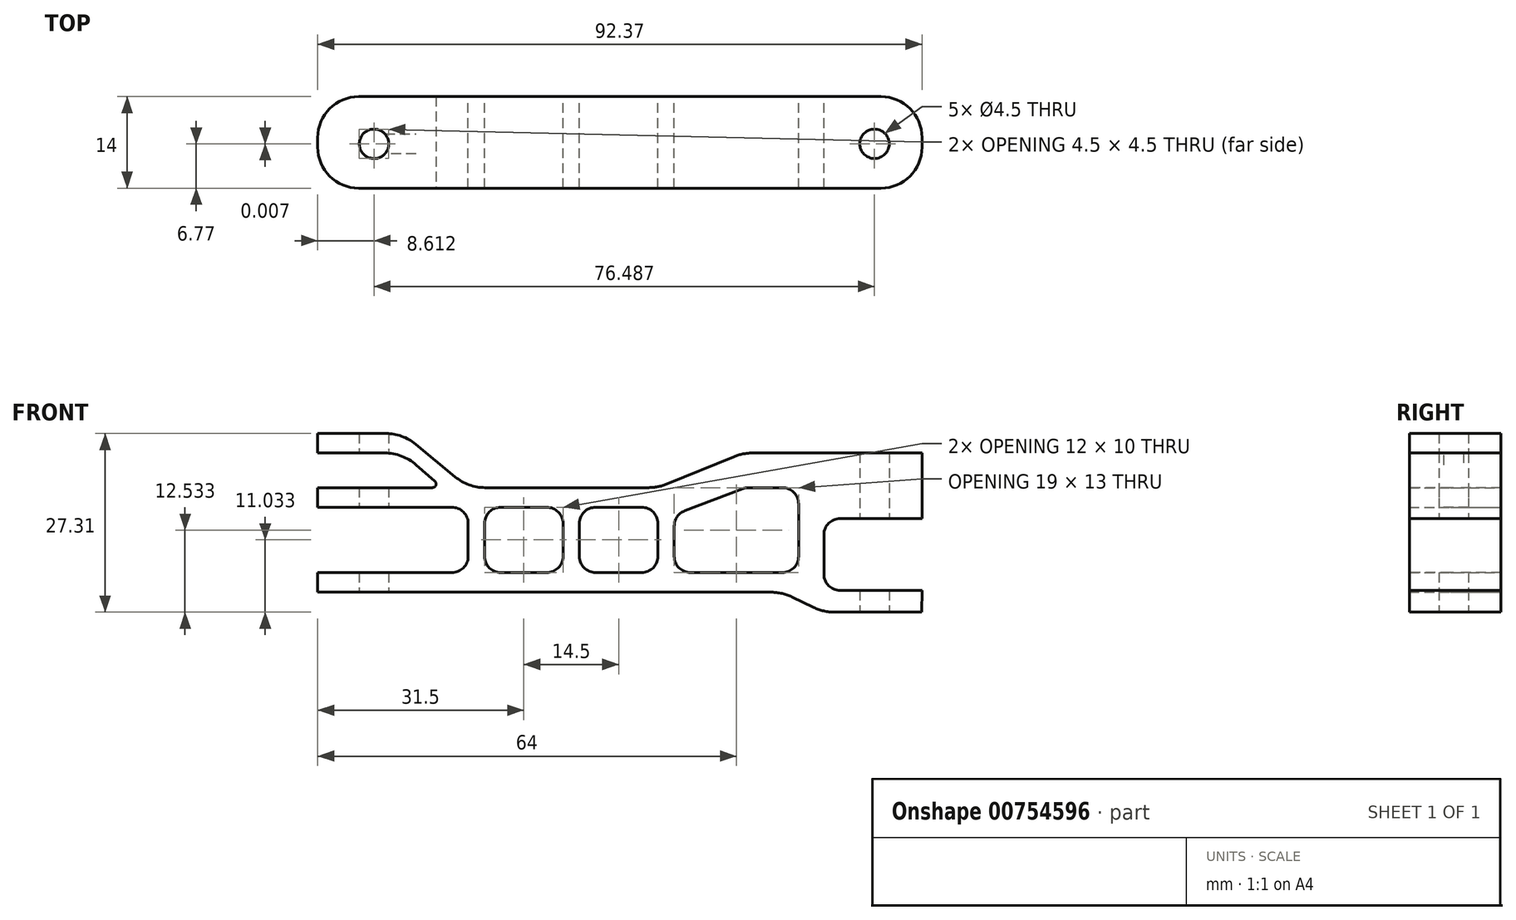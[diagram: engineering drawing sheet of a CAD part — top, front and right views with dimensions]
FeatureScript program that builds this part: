
annotation { "Feature Type Name" : "Feature", "Feature Type Description" : "" }
export const myFeature = defineFeature(function(context is Context, id is Id, definition is map)
    precondition{}
    {
        {
            var Q0;
            Q0=qCreatedBy(makeId("Front.planeOp"),FACE);
            var sketch = newSketch(context, id + "F0", { "sketchPlane" : qUnion([Q0])});
            skLineSegment(sketch, "E0", {"start": v(74.63, 0) * mm, "end": v(59.63, 0) * mm});
            skLineSegment(sketch, "E1", {"start": v(59.63, 0) * mm, "end": v(53.32, 3.03) * mm});
            skLineSegment(sketch, "E2", {"start": v(53.32, 3.03) * mm, "end": v(-17.68, 3.03) * mm});
            skLineSegment(sketch, "E3", {"start": v(-17.68, 3.03) * mm, "end": v(-17.68, 6.03) * mm});
            skLineSegment(sketch, "E4", {"start": v(-17.68, 6.03) * mm, "end": v(5.32, 6.03) * mm});
            skLineSegment(sketch, "E5", {"start": v(5.32, 6.03) * mm, "end": v(5.32, 16.03) * mm});
            skLineSegment(sketch, "E6", {"start": v(5.32, 16.03) * mm, "end": v(-17.68, 16.03) * mm});
            skLineSegment(sketch, "E7", {"start": v(-17.68, 16.03) * mm, "end": v(-17.68, 19.03) * mm});
            skLineSegment(sketch, "E8", {"start": v(-17.68, 19.03) * mm, "end": v(1.32, 19.03) * mm});
            skLineSegment(sketch, "E9", {"start": v(1.32, 19.03) * mm, "end": v(-4.7, 24.31) * mm});
            skLineSegment(sketch, "E10", {"start": v(-4.7, 24.31) * mm, "end": v(-17.68, 24.31) * mm});
            skLineSegment(sketch, "E11", {"start": v(-17.68, 24.31) * mm, "end": v(-17.68, 27.31) * mm});
            skLineSegment(sketch, "E12", {"start": v(-17.68, 27.31) * mm, "end": v(-4.7, 27.31) * mm});
            skLineSegment(sketch, "E13", {"start": v(-4.7, 27.31) * mm, "end": v(5.32, 19.03) * mm});
            skLineSegment(sketch, "E14", {"start": v(5.32, 19.03) * mm, "end": v(34.32, 19.03) * mm});
            skLineSegment(sketch, "E15", {"start": v(34.32, 19.03) * mm, "end": v(47.29, 24.31) * mm});
            skLineSegment(sketch, "E16", {"start": v(47.29, 24.31) * mm, "end": v(74.69, 24.31) * mm});
            skLineSegment(sketch, "E17", {"start": v(74.69, 24.31) * mm, "end": v(74.69, 14.31) * mm});
            skLineSegment(sketch, "E18", {"start": v(74.69, 3.31) * mm, "end": v(74.63, 0) * mm});
            skLineSegment(sketch, "E19", {"start": v(7.82, 16.03) * mm, "end": v(7.82, 6.03) * mm});
            skLineSegment(sketch, "E20", {"start": v(7.82, 6.03) * mm, "end": v(19.82, 6.03) * mm});
            skLineSegment(sketch, "E21", {"start": v(19.82, 6.03) * mm, "end": v(19.82, 16.03) * mm});
            skLineSegment(sketch, "E22", {"start": v(19.82, 16.03) * mm, "end": v(7.82, 16.03) * mm});
            skLineSegment(sketch, "E23", {"start": v(22.32, 16.03) * mm, "end": v(22.32, 6.03) * mm});
            skLineSegment(sketch, "E24", {"start": v(22.32, 6.03) * mm, "end": v(34.32, 6.03) * mm});
            skLineSegment(sketch, "E25", {"start": v(34.32, 6.03) * mm, "end": v(34.32, 16.03) * mm});
            skLineSegment(sketch, "E26", {"start": v(34.32, 16.03) * mm, "end": v(22.32, 16.03) * mm});
            skLineSegment(sketch, "E27", {"start": v(36.82, 6.03) * mm, "end": v(55.82, 6.03) * mm});
            skLineSegment(sketch, "E28", {"start": v(55.82, 6.03) * mm, "end": v(55.82, 19.03) * mm});
            skLineSegment(sketch, "E29", {"start": v(55.82, 19.03) * mm, "end": v(47.74, 19.03) * mm});
            skLineSegment(sketch, "E30", {"start": v(47.74, 19.03) * mm, "end": v(36.82, 14.87) * mm});
            skLineSegment(sketch, "E31", {"start": v(36.82, 14.87) * mm, "end": v(36.82, 6.03) * mm});
            skLineSegment(sketch, "E32", {"start": v(74.69, 14.31) * mm, "end": v(59.69, 14.31) * mm});
            skLineSegment(sketch, "E33", {"start": v(74.69, 3.31) * mm, "end": v(59.69, 3.31) * mm});
            skLineSegment(sketch, "E34", {"start": v(59.69, 3.31) * mm, "end": v(59.69, 14.31) * mm});
            skSolve(sketch);
        }
        {
            var Q0;
            Q0=makeQuery(id+"F0.imprint","IMPRINT",FACE,{"disambiguationData":[TD([[makeQuery(id+"F0.imprint","IMPRINT",EDGE,{"derivedFrom":sQuery(id+"F0.wireOp",EDGE,"E0")}),-1.0]])]});
            extrude(context, id + "F1", {"entities" : qUnion([Q0]), "depth" : 14 * mm, "offsetDistance" : 25 * mm});
        }
        {
            var Q0;
            Q0=qCreatedBy(makeId("Top.planeOp"),FACE);
            var sketch = newSketch(context, id + "F2", { "sketchPlane" : qUnion([Q0])});
            skCircle(sketch, "E35", {"center": v(-9.07, -7.23) * mm, "radius": 2.25 * mm});
            skCircle(sketch, "E36", {"center": v(67.42, -7.22) * mm, "radius": 2.25 * mm});
            skSolve(sketch);
        }
        {
            var Q0;
            Q0 = qSketchRegion(id + "F2", true);
            extrude(context, id + "F3", {"entities" : qUnion([Q0]), "operationType" : NewBodyOperationType.REMOVE, "depth" : 99.1 * mm, "offsetDistance" : 25 * mm});
        }
        {
            var Q0;
            Q0 = qSketchRegion(id + "F2", true);
            extrude(context, id + "F4", {"entities" : qUnion([Q0]), "operationType" : NewBodyOperationType.REMOVE, "oppositeDirection" : true, "depth" : 25 * mm, "offsetDistance" : 25 * mm});
        }
        {
            var Q0;
            Q0=makeQuery(id+"F1.opExtrude","CAP_EDGE",EDGE,{"disambiguationData":[OSD([sQuery(id+"F0.wireOp",EDGE,"E11")])],"isStart":false});
            var Q1;
            Q1=makeQuery(id+"F1.opExtrude","CAP_EDGE",EDGE,{"disambiguationData":[OSD([sQuery(id+"F0.wireOp",EDGE,"E11")])],"isStart":true});
            var Q2;
            Q2=makeQuery(id+"F1.opExtrude","CAP_EDGE",EDGE,{"disambiguationData":[OSD([sQuery(id+"F0.wireOp",EDGE,"E7")])],"isStart":false});
            var Q3;
            Q3=makeQuery(id+"F1.opExtrude","CAP_EDGE",EDGE,{"disambiguationData":[OSD([sQuery(id+"F0.wireOp",EDGE,"E7")])],"isStart":true});
            var Q4;
            Q4=makeQuery(id+"F1.opExtrude","CAP_EDGE",EDGE,{"disambiguationData":[OSD([sQuery(id+"F0.wireOp",EDGE,"E3")])],"isStart":true});
            var Q5;
            Q5=makeQuery(id+"F1.opExtrude","CAP_EDGE",EDGE,{"disambiguationData":[OSD([sQuery(id+"F0.wireOp",EDGE,"E3")])],"isStart":false});
            fillet(context, id + "F5", {"entities" : qUnion([Q0, Q1, Q2, Q3, Q4, Q5]), "radius" : 6.28 * mm, "tangentPropagation" : true, "allowEdgeOverflow" : false});
        }
        {
            var Q0;
            Q0=makeQuery(id+"F1.opExtrude","CAP_EDGE",EDGE,{"disambiguationData":[OSD([sQuery(id+"F0.wireOp",EDGE,"E17")])],"isStart":false});
            var Q1;
            Q1=makeQuery(id+"F1.opExtrude","CAP_EDGE",EDGE,{"disambiguationData":[OSD([sQuery(id+"F0.wireOp",EDGE,"E17")])],"isStart":true});
            var Q2;
            Q2=makeQuery(id+"F1.opExtrude","CAP_EDGE",EDGE,{"disambiguationData":[OSD([sQuery(id+"F0.wireOp",EDGE,"E18")])],"isStart":false});
            var Q3;
            Q3=makeQuery(id+"F1.opExtrude","CAP_EDGE",EDGE,{"disambiguationData":[OSD([sQuery(id+"F0.wireOp",EDGE,"E18")])],"isStart":true});
            fillet(context, id + "F6", {"entities" : qUnion([Q0, Q1, Q2, Q3]), "radius" : 6.28 * mm, "tangentPropagation" : true, "allowEdgeOverflow" : false});
        }
        {
            var Q0;
            Q0=makeQuery(id+"F1.opExtrude","SWEPT_EDGE",EDGE,{"disambiguationData":[OSD([sQuery(id+"F0.wireOp",EDGE,"E27"),sQuery(id+"F0.wireOp",EDGE,"E31")])]});
            var Q1;
            Q1=makeQuery(id+"F1.opExtrude","SWEPT_EDGE",EDGE,{"disambiguationData":[OSD([sQuery(id+"F0.wireOp",EDGE,"E30"),sQuery(id+"F0.wireOp",EDGE,"E31")])]});
            var Q2;
            Q2=makeQuery(id+"F1.opExtrude","SWEPT_EDGE",EDGE,{"disambiguationData":[OSD([sQuery(id+"F0.wireOp",EDGE,"E29"),sQuery(id+"F0.wireOp",EDGE,"E30")])]});
            var Q3;
            Q3=makeQuery(id+"F1.opExtrude","SWEPT_EDGE",EDGE,{"disambiguationData":[OSD([sQuery(id+"F0.wireOp",EDGE,"E28"),sQuery(id+"F0.wireOp",EDGE,"E29")])]});
            var Q4;
            Q4=makeQuery(id+"F1.opExtrude","SWEPT_EDGE",EDGE,{"disambiguationData":[OSD([sQuery(id+"F0.wireOp",EDGE,"E27"),sQuery(id+"F0.wireOp",EDGE,"E28")])]});
            fillet(context, id + "F7", {"entities" : qUnion([Q0, Q1, Q2, Q3, Q4]), "radius" : 2.5 * mm, "tangentPropagation" : true, "allowEdgeOverflow" : false});
        }
        {
            var Q0;
            Q0=makeQuery(id+"F1.opExtrude","SWEPT_EDGE",EDGE,{"disambiguationData":[OSD([sQuery(id+"F0.wireOp",EDGE,"E25"),sQuery(id+"F0.wireOp",EDGE,"E26")])]});
            var Q1;
            Q1=makeQuery(id+"F1.opExtrude","SWEPT_EDGE",EDGE,{"disambiguationData":[OSD([sQuery(id+"F0.wireOp",EDGE,"E23"),sQuery(id+"F0.wireOp",EDGE,"E26")])]});
            var Q2;
            Q2=makeQuery(id+"F1.opExtrude","SWEPT_EDGE",EDGE,{"disambiguationData":[OSD([sQuery(id+"F0.wireOp",EDGE,"E23"),sQuery(id+"F0.wireOp",EDGE,"E24")])]});
            var Q3;
            Q3=makeQuery(id+"F1.opExtrude","SWEPT_EDGE",EDGE,{"disambiguationData":[OSD([sQuery(id+"F0.wireOp",EDGE,"E24"),sQuery(id+"F0.wireOp",EDGE,"E25")])]});
            fillet(context, id + "F8", {"entities" : qUnion([Q0, Q1, Q2, Q3]), "radius" : 2.5 * mm, "tangentPropagation" : true, "allowEdgeOverflow" : false});
        }
        {
            var Q0;
            Q0=makeQuery(id+"F1.opExtrude","SWEPT_EDGE",EDGE,{"disambiguationData":[OSD([sQuery(id+"F0.wireOp",EDGE,"E21"),sQuery(id+"F0.wireOp",EDGE,"E22")])]});
            var Q1;
            Q1=makeQuery(id+"F1.opExtrude","SWEPT_EDGE",EDGE,{"disambiguationData":[OSD([sQuery(id+"F0.wireOp",EDGE,"E19"),sQuery(id+"F0.wireOp",EDGE,"E22")])]});
            var Q2;
            Q2=makeQuery(id+"F1.opExtrude","SWEPT_EDGE",EDGE,{"disambiguationData":[OSD([sQuery(id+"F0.wireOp",EDGE,"E19"),sQuery(id+"F0.wireOp",EDGE,"E20")])]});
            var Q3;
            Q3=makeQuery(id+"F1.opExtrude","SWEPT_EDGE",EDGE,{"disambiguationData":[OSD([sQuery(id+"F0.wireOp",EDGE,"E20"),sQuery(id+"F0.wireOp",EDGE,"E21")])]});
            fillet(context, id + "F9", {"entities" : qUnion([Q0, Q1, Q2, Q3]), "radius" : 2.5 * mm, "tangentPropagation" : true, "allowEdgeOverflow" : false});
        }
        {
            var Q0;
            Q0=makeQuery(id+"F1.opExtrude","SWEPT_EDGE",EDGE,{"disambiguationData":[OSD([sQuery(id+"F0.wireOp",EDGE,"E5"),sQuery(id+"F0.wireOp",EDGE,"E6")])]});
            var Q1;
            Q1=makeQuery(id+"F1.opExtrude","SWEPT_EDGE",EDGE,{"disambiguationData":[OSD([sQuery(id+"F0.wireOp",EDGE,"E4"),sQuery(id+"F0.wireOp",EDGE,"E5")])]});
            var Q2;
            Q2=makeQuery(id+"F1.opExtrude","SWEPT_EDGE",EDGE,{"disambiguationData":[OSD([sQuery(id+"F0.wireOp",EDGE,"E32"),sQuery(id+"F0.wireOp",EDGE,"E34")])]});
            var Q3;
            Q3=makeQuery(id+"F1.opExtrude","SWEPT_EDGE",EDGE,{"disambiguationData":[OSD([sQuery(id+"F0.wireOp",EDGE,"E33"),sQuery(id+"F0.wireOp",EDGE,"E34")])]});
            fillet(context, id + "F10", {"entities" : qUnion([Q0, Q1, Q2, Q3]), "radius" : 2.5 * mm, "tangentPropagation" : true, "allowEdgeOverflow" : false});
        }
        {
            var Q0;
            Q0=makeQuery(id+"F1.opExtrude","SWEPT_EDGE",EDGE,{"disambiguationData":[OSD([sQuery(id+"F0.wireOp",EDGE,"E15"),sQuery(id+"F0.wireOp",EDGE,"E16")])]});
            var Q1;
            Q1=makeQuery(id+"F1.opExtrude","SWEPT_EDGE",EDGE,{"disambiguationData":[OSD([sQuery(id+"F0.wireOp",EDGE,"E14"),sQuery(id+"F0.wireOp",EDGE,"E15")])]});
            var Q2;
            Q2=makeQuery(id+"F1.opExtrude","SWEPT_EDGE",EDGE,{"disambiguationData":[OSD([sQuery(id+"F0.wireOp",EDGE,"E13"),sQuery(id+"F0.wireOp",EDGE,"E14")])]});
            var Q3;
            Q3=makeQuery(id+"F1.opExtrude","SWEPT_EDGE",EDGE,{"disambiguationData":[OSD([sQuery(id+"F0.wireOp",EDGE,"E12"),sQuery(id+"F0.wireOp",EDGE,"E13")])]});
            fillet(context, id + "F11", {"entities" : qUnion([Q0, Q1, Q2, Q3]), "radius" : 7.2 * mm, "tangentPropagation" : true, "allowEdgeOverflow" : false});
        }
        {
            var Q0;
            Q0=makeQuery(id+"F1.opExtrude","SWEPT_EDGE",EDGE,{"disambiguationData":[OSD([sQuery(id+"F0.wireOp",EDGE,"E1"),sQuery(id+"F0.wireOp",EDGE,"E2")])]});
            var Q1;
            Q1=makeQuery(id+"F1.opExtrude","SWEPT_EDGE",EDGE,{"disambiguationData":[OSD([sQuery(id+"F0.wireOp",EDGE,"E0"),sQuery(id+"F0.wireOp",EDGE,"E1")])]});
            fillet(context, id + "F12", {"entities" : qUnion([Q0, Q1]), "radius" : 7.2 * mm, "tangentPropagation" : true, "allowEdgeOverflow" : false});
        }
        {
            var Q0;
            Q0=makeQuery(id+"F1.opExtrude","SWEPT_EDGE",EDGE,{"disambiguationData":[OSD([sQuery(id+"F0.wireOp",EDGE,"E9"),sQuery(id+"F0.wireOp",EDGE,"E10")])]});
            fillet(context, id + "F13", {"entities" : qUnion([Q0]), "radius" : 7.2 * mm, "tangentPropagation" : true, "allowEdgeOverflow" : false});
        }
        {
            var Q0;
            Q0=makeQuery(id+"F1.opExtrude","SWEPT_EDGE",EDGE,{"disambiguationData":[OSD([sQuery(id+"F0.wireOp",EDGE,"E8"),sQuery(id+"F0.wireOp",EDGE,"E9")])]});
            fillet(context, id + "F14", {"entities" : qUnion([Q0]), "radius" : 0.54 * mm, "tangentPropagation" : true, "allowEdgeOverflow" : false});
        }
    });
